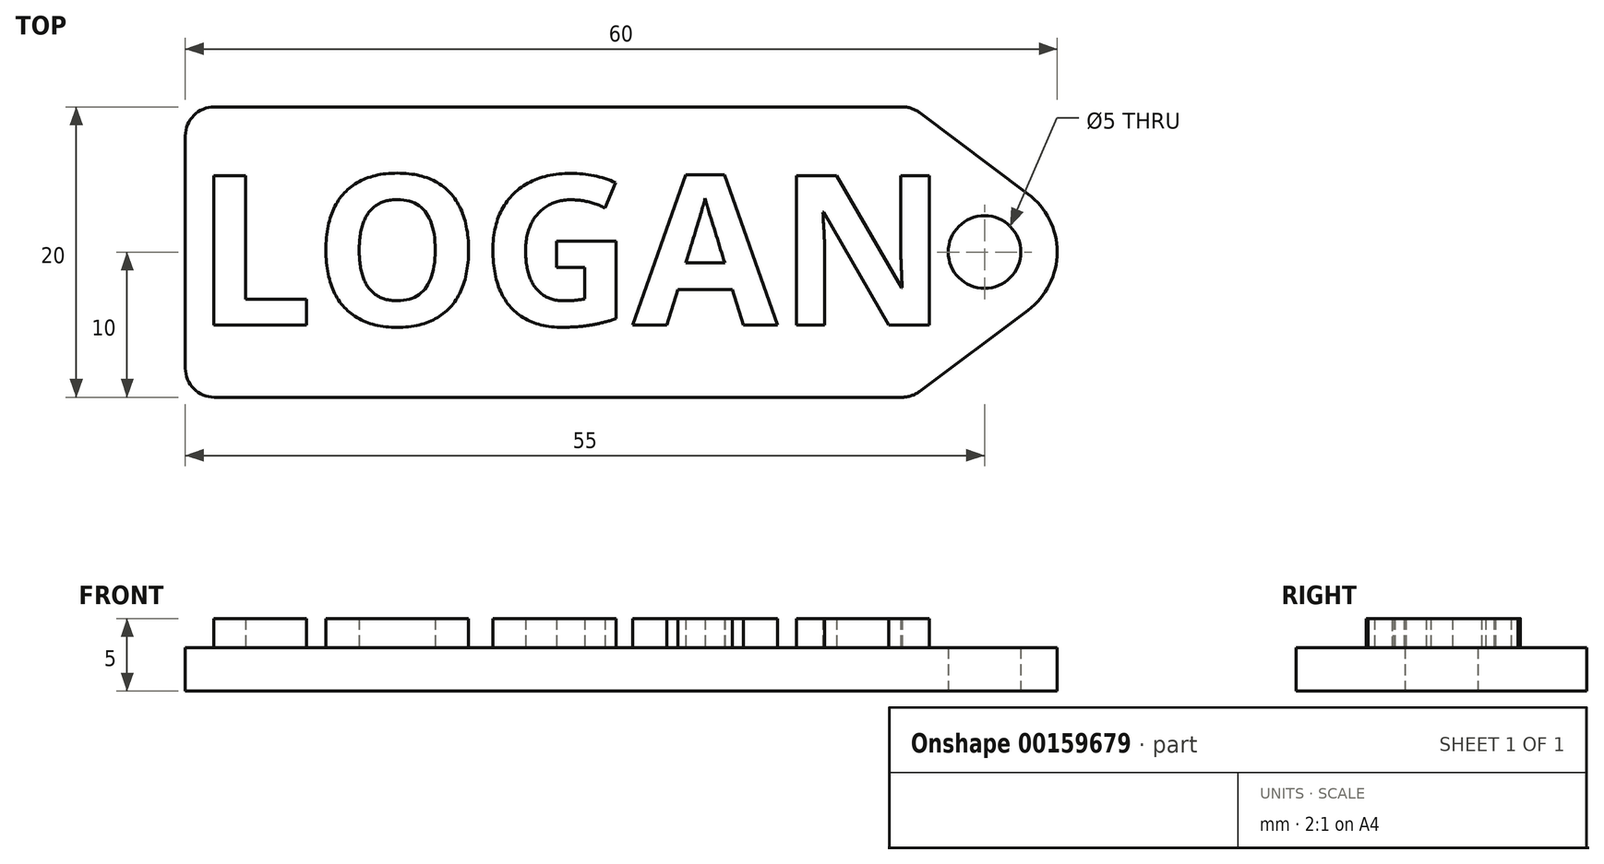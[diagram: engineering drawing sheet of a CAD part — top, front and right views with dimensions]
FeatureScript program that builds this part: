
annotation { "Feature Type Name" : "Feature", "Feature Type Description" : "" }
export const myFeature = defineFeature(function(context is Context, id is Id, definition is map)
    precondition{}
    {
        {
            var Q0;
            Q0=qCreatedBy(makeId("Top.planeOp"),FACE);
            var sketch = newSketch(context, id + "F0", { "sketchPlane" : qUnion([Q0])});
            skLineSegment(sketch, "E0.bottom", {"start": v(24.33, -10) * mm, "end": v(-23, -10) * mm});
            skLineSegment(sketch, "E0.top", {"start": v(24.33, 10) * mm, "end": v(-23, 10) * mm});
            skLineSegment(sketch, "E0.left", {"start": v(25, -10) * mm, "end": v(25, 10) * mm, "construction": true});
            skLineSegment(sketch, "E0.right", {"start": v(-25, -8) * mm, "end": v(-25, 8) * mm});
            skPoint(sketch, "E0.middle", {"position": v(0, 0) * mm});
            skCircle(sketch, "E1", {"center": v(30, 0) * mm, "radius": 2.5 * mm});
            skLineSegment(sketch, "E2", {"start": v(25.53, 9.6) * mm, "end": v(33, 4) * mm});
            skArc(sketch, "E3", {"start": v(35, 0) * mm, "mid": v(34.47, 2.24) * mm, "end": v(33, 4) * mm});
            skLineSegment(sketch, "E4.MirrorCS", {"start": v(25.53, -9.6) * mm, "end": v(33, -4) * mm});
            skArc(sketch, "E5.MirrorCS", {"start": v(35, 0) * mm, "mid": v(34.47, -2.24) * mm, "end": v(33, -4) * mm});
            skPoint(sketch, "E6.visualSharp", {"position": v(-25, 10) * mm});
            skArc(sketch, "E6.filletArc", {"start": v(-23, 10) * mm, "mid": v(-24.41, 9.41) * mm, "end": v(-25, 8) * mm});
            skPoint(sketch, "E7.visualSharp", {"position": v(-25, -10) * mm});
            skArc(sketch, "E7.filletArc", {"start": v(-25, -8) * mm, "mid": v(-24.41, -9.41) * mm, "end": v(-23, -10) * mm});
            skPoint(sketch, "E8.visualSharp", {"position": v(25, 10) * mm});
            skArc(sketch, "E8.filletArc", {"start": v(25.53, 9.6) * mm, "mid": v(24.97, 9.9) * mm, "end": v(24.33, 10) * mm});
            skPoint(sketch, "E9.visualSharp", {"position": v(25, -10) * mm});
            skArc(sketch, "E9.filletArc", {"start": v(24.33, -10) * mm, "mid": v(24.97, -9.9) * mm, "end": v(25.53, -9.6) * mm});
            skSolve(sketch);
        }
        {
            var Q0;
            Q0=makeQuery(id+"F0.imprint","IMPRINT",FACE,{"disambiguationData":[TD([[makeQuery(id+"F0.imprint","IMPRINT",EDGE,{"derivedFrom":sQuery(id+"F0.wireOp",EDGE,"E0.bottom")}),-1.0]])]});
            extrude(context, id + "F1", {"entities" : qUnion([Q0]), "depth" : 3 * mm});
        }
        {
            var Q0;
            Q0=makeQuery(id+"F1.opExtrude","CAP_FACE",FACE,{"disambiguationData":[OSD([sQuery(id+"F0.wireOp",EDGE,"E0.bottom"),sQuery(id+"F0.wireOp",EDGE,"E0.top"),sQuery(id+"F0.wireOp",EDGE,"E0.right"),sQuery(id+"F0.wireOp",EDGE,"E1"),sQuery(id+"F0.wireOp",EDGE,"E2"),sQuery(id+"F0.wireOp",EDGE,"E3"),sQuery(id+"F0.wireOp",EDGE,"E4.MirrorCS"),sQuery(id+"F0.wireOp",EDGE,"E5.MirrorCS"),sQuery(id+"F0.wireOp",EDGE,"E6.filletArc"),sQuery(id+"F0.wireOp",EDGE,"E7.filletArc"),sQuery(id+"F0.wireOp",EDGE,"E8.filletArc"),sQuery(id+"F0.wireOp",EDGE,"E9.filletArc")])],"isStart":false});
            var sketch = newSketch(context, id + "F2", { "sketchPlane" : qUnion([Q0])});
            skText(sketch, "E10", { "text": "LOGAN", "fontName": "OpenSans-Bold.ttf"});
            const initialGuessF2  = {"E10": [-0.02433, -0.00504, 1, 0, 0.0104]};
            skSetInitialGuess(sketch, initialGuessF2);
            skSolve(sketch);
        }
        {
            var Q0;
            Q0 = qSketchRegion(id + "F2", true);
            extrude(context, id + "F3", {"entities" : qUnion([Q0]), "operationType" : NewBodyOperationType.ADD, "depth" : 2 * mm});
        }
    });
